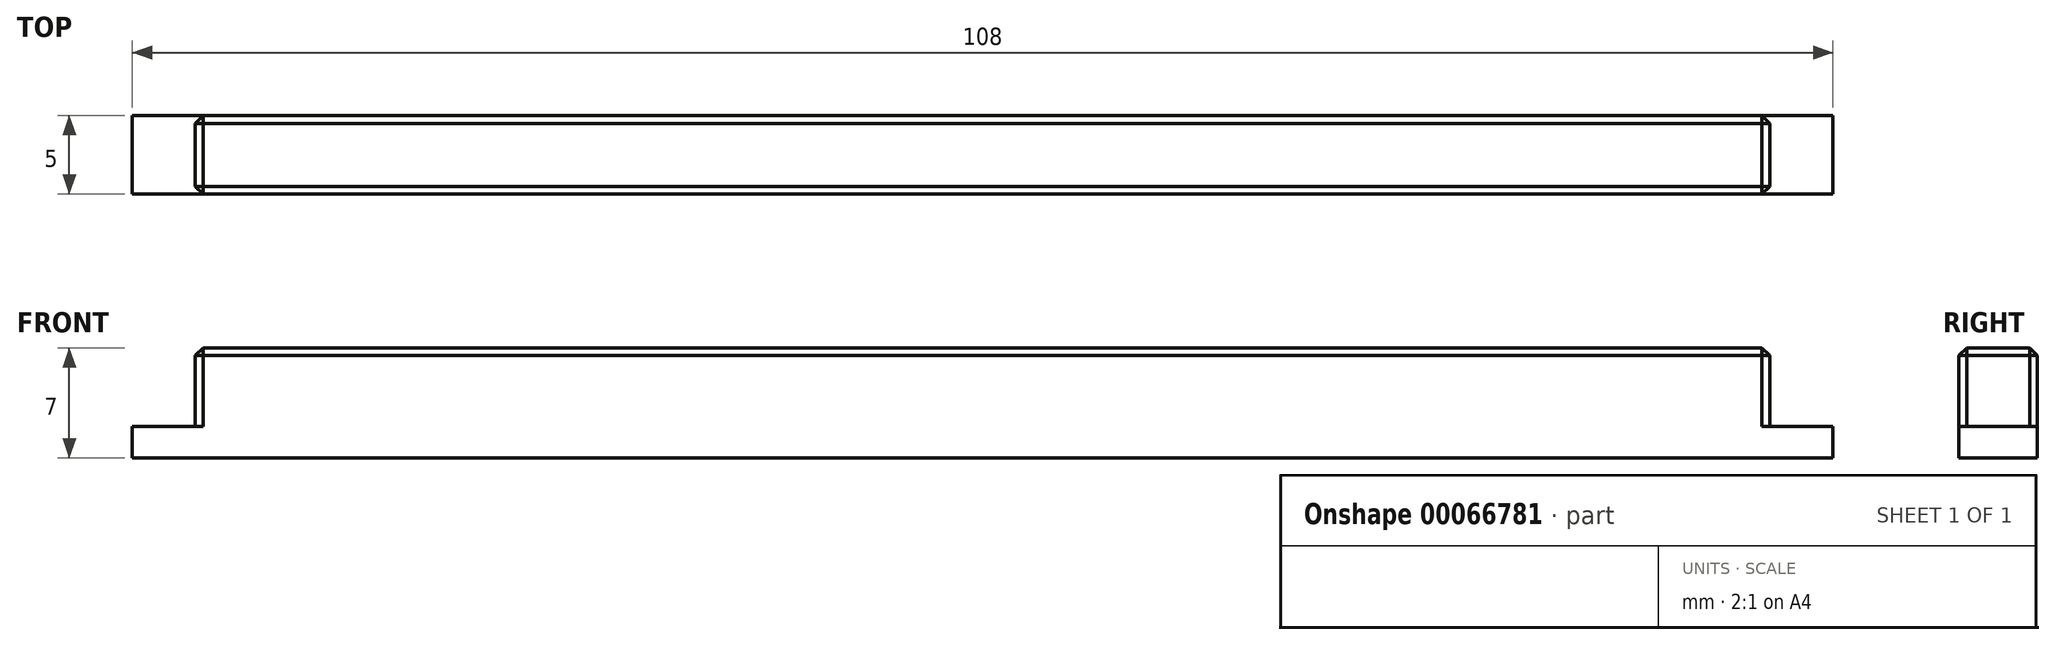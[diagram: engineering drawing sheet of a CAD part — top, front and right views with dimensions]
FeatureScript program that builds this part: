
annotation { "Feature Type Name" : "Feature", "Feature Type Description" : "" }
export const myFeature = defineFeature(function(context is Context, id is Id, definition is map)
    precondition{}
    {
        {
            var Q0;
            Q0=qCreatedBy(makeId("Top.planeOp"),FACE);
            var sketch = newSketch(context, id + "F0", { "sketchPlane" : qUnion([Q0])});
            skLineSegment(sketch, "E0.bottom", {"start": v(-46.16, 0) * mm, "end": v(53.84, 0) * mm});
            skLineSegment(sketch, "E0.top", {"start": v(-46.16, 5) * mm, "end": v(53.84, 5) * mm});
            skLineSegment(sketch, "E0.left", {"start": v(-46.16, 0) * mm, "end": v(-46.16, 5) * mm});
            skLineSegment(sketch, "E0.right", {"start": v(53.84, 0) * mm, "end": v(53.84, 5) * mm});
            skLineSegment(sketch, "E1.bottom", {"start": v(-46.16, 5) * mm, "end": v(-50.16, 5) * mm});
            skLineSegment(sketch, "E1.top", {"start": v(-46.16, 0) * mm, "end": v(-50.16, 0) * mm});
            skLineSegment(sketch, "E1.left", {"start": v(-46.16, 5) * mm, "end": v(-46.16, 0) * mm});
            skLineSegment(sketch, "E1.right", {"start": v(-50.16, 5) * mm, "end": v(-50.16, 0) * mm});
            skLineSegment(sketch, "E2.bottom", {"start": v(53.84, 5) * mm, "end": v(57.84, 5) * mm});
            skLineSegment(sketch, "E2.top", {"start": v(53.84, 0) * mm, "end": v(57.84, 0) * mm});
            skLineSegment(sketch, "E2.left", {"start": v(53.84, 5) * mm, "end": v(53.84, 0) * mm});
            skLineSegment(sketch, "E2.right", {"start": v(57.84, 5) * mm, "end": v(57.84, 0) * mm});
            skSolve(sketch);
        }
        {
            var Q0;
            Q0=makeQuery(id+"F0.imprint","IMPRINT",FACE,{"disambiguationData":[TD([[makeQuery(id+"F0.imprint","IMPRINT",EDGE,{"derivedFrom":sQuery(id+"F0.wireOp",EDGE,"E0.bottom")}),1.0]])]});
            extrude(context, id + "F1", {"entities" : qUnion([Q0]), "depth" : 5 * mm});
        }
        {
            var Q0;
            Q0=makeQuery(id+"F0.imprint","IMPRINT",FACE,{"disambiguationData":[TD([[makeQuery(id+"F0.imprint","IMPRINT",EDGE,{"derivedFrom":sQuery(id+"F0.wireOp",EDGE,"E1.bottom")}),1.0]])]});
            var Q1;
            Q1=makeQuery(id+"F0.imprint","IMPRINT",FACE,{"disambiguationData":[TD([[makeQuery(id+"F0.imprint","IMPRINT",EDGE,{"derivedFrom":sQuery(id+"F0.wireOp",EDGE,"E0.bottom")}),1.0]])]});
            var Q2;
            Q2=makeQuery(id+"F0.imprint","IMPRINT",FACE,{"disambiguationData":[TD([[makeQuery(id+"F0.imprint","IMPRINT",EDGE,{"derivedFrom":sQuery(id+"F0.wireOp",EDGE,"E2.bottom")}),-1.0]])]});
            extrude(context, id + "F2", {"entities" : qUnion([Q0, Q1, Q2]), "operationType" : NewBodyOperationType.ADD, "oppositeDirection" : true, "depth" : 2 * mm});
        }
        {
            var Q0;
            Q0=makeQuery(id+"F1.opExtrude","CAP_FACE",FACE,{"disambiguationData":[OSD([sQuery(id+"F0.wireOp",EDGE,"E0.bottom"),sQuery(id+"F0.wireOp",EDGE,"E0.top"),sQuery(id+"F0.wireOp",EDGE,"E1.left"),sQuery(id+"F0.wireOp",EDGE,"E2.left")])],"isStart":false});
            var Q1;
            Q1=makeQuery(id+"F1.opExtrude","SWEPT_EDGE",EDGE,{"disambiguationData":[OSD([sQuery(id+"F0.wireOp",EDGE,"E0.top"),sQuery(id+"F0.wireOp",EDGE,"E2.bottom"),sQuery(id+"F0.wireOp",EDGE,"E2.left")])]});
            var Q2;
            Q2=makeQuery(id+"F1.opExtrude","SWEPT_EDGE",EDGE,{"disambiguationData":[OSD([sQuery(id+"F0.wireOp",EDGE,"E0.bottom"),sQuery(id+"F0.wireOp",EDGE,"E2.top"),sQuery(id+"F0.wireOp",EDGE,"E2.left")])]});
            var Q3;
            Q3=makeQuery(id+"F1.opExtrude","SWEPT_EDGE",EDGE,{"disambiguationData":[OSD([sQuery(id+"F0.wireOp",EDGE,"E0.bottom"),sQuery(id+"F0.wireOp",EDGE,"E1.top"),sQuery(id+"F0.wireOp",EDGE,"E1.left")])]});
            var Q4;
            Q4=makeQuery(id+"F1.opExtrude","SWEPT_EDGE",EDGE,{"disambiguationData":[OSD([sQuery(id+"F0.wireOp",EDGE,"E0.top"),sQuery(id+"F0.wireOp",EDGE,"E1.bottom"),sQuery(id+"F0.wireOp",EDGE,"E1.left")])]});
            chamfer(context, id + "F3", {"entities" : qUnion([Q0, Q1, Q2, Q3, Q4]), "width" : .5 * mm, "tangentPropagation" : true});
        }
    });
